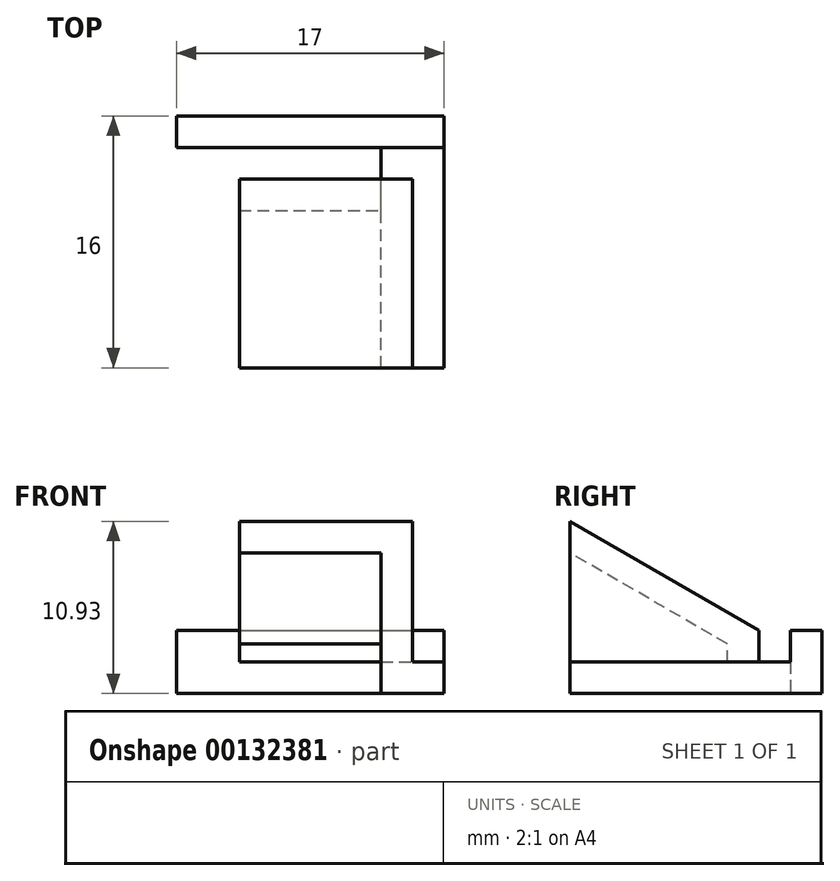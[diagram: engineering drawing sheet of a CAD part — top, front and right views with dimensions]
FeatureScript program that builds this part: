
annotation { "Feature Type Name" : "Feature", "Feature Type Description" : "" }
export const myFeature = defineFeature(function(context is Context, id is Id, definition is map)
    precondition{}
    {
        {
            var Q0;
            Q0=qCreatedBy(makeId("Top.planeOp"),FACE);
            var sketch = newSketch(context, id + "F0", { "sketchPlane" : qUnion([Q0])});
            skCircle(sketch, "E0", {"center": v(0, 0) * mm, "radius": 2.5 * mm});
            skPoint(sketch, "E1", {"position": v(2.5, 0) * mm});
            skPoint(sketch, "E2", {"position": v(-2.5, 0) * mm});
            skLineSegment(sketch, "E3", {"start": v(-2.5, 0) * mm, "end": v(-4.5, 0) * mm, "construction": true});
            skLineSegment(sketch, "E4", {"start": v(2.5, 0) * mm, "end": v(4.5, 0) * mm, "construction": true});
            skPoint(sketch, "E5", {"position": v(0, 2.5) * mm});
            skPoint(sketch, "E6", {"position": v(0, -2.5) * mm});
            skSolve(sketch);
        }
        {
            var Q0;
            Q0=sQuery(id+"F0.wireOp",VERTEX,"E4.end");
            var Q1;
            Q1=qCreatedBy(makeId("Right.planeOp"),FACE);
            cPlane(context, id + "F1", {"entities" : qUnion([Q0, Q1]), "cplaneType" : CPlaneType.PLANE_POINT, "offset" : 25 * mm, "width" : 150 * mm, "height" : 150 * mm});
        }
        {
            var Q0;
            Q0=sQuery(id+"F0.wireOp",VERTEX,"E3.end");
            var Q1;
            Q1=qCreatedBy(makeId("Right.planeOp"),FACE);
            cPlane(context, id + "F2", {"entities" : qUnion([Q0, Q1]), "cplaneType" : CPlaneType.PLANE_POINT, "offset" : 25 * mm, "width" : 150 * mm, "height" : 150 * mm});
        }
        {
            var Q0;
            Q0=qCreatedBy(id+"F1.planeOp",FACE);
            var sketch = newSketch(context, id + "F3", { "sketchPlane" : qUnion([Q0])});
            skLineSegment(sketch, "E7", {"start": v(6.5, 0) * mm, "end": v(6.5, 4) * mm});
            skLineSegment(sketch, "E8", {"start": v(6.5, 4) * mm, "end": v(-5.5, 10.93) * mm});
            skLineSegment(sketch, "E9", {"start": v(-5.5, 10.93) * mm, "end": v(-5.5, 8.93) * mm});
            skLineSegment(sketch, "E10", {"start": v(-5.5, 8.93) * mm, "end": v(4.5, 3.15) * mm});
            skLineSegment(sketch, "E11", {"start": v(4.5, 3.15) * mm, "end": v(4.5, 0) * mm});
            skLineSegment(sketch, "E12", {"start": v(4.5, 0) * mm, "end": v(6.5, 0) * mm});
            skSolve(sketch);
        }
        {
            var Q0;
            Q0 = qSketchRegion(id + "F3", true);
            var Q1;
            Q1=qCreatedBy(id+"F2.planeOp",FACE);
            extrude(context, id + "F4", {"entities" : qUnion([Q0]), "endBound" : BoundingType.UP_TO_SURFACE, "oppositeDirection" : true, "endBoundEntityFace" : qUnion([Q1]), "depth" : 25 * mm});
        }
        {
            var Q0;
            Q0=makeQuery(id+"F4.opExtrude","CAP_FACE",FACE,{"disambiguationData":[OSD([sQuery(id+"F3.wireOp",EDGE,"E7"),sQuery(id+"F3.wireOp",EDGE,"E8"),sQuery(id+"F3.wireOp",EDGE,"E9"),sQuery(id+"F3.wireOp",EDGE,"E10"),sQuery(id+"F3.wireOp",EDGE,"E11"),sQuery(id+"F3.wireOp",EDGE,"E12")])],"isStart":true});
            var sketch = newSketch(context, id + "F5", { "sketchPlane" : qUnion([Q0])});
            skLineSegment(sketch, "E13", {"start": v(-5.5, 10.93) * mm, "end": v(6.5, 4) * mm});
            skLineSegment(sketch, "E14", {"start": v(6.5, 4) * mm, "end": v(6.5, 0) * mm});
            skLineSegment(sketch, "E15", {"start": v(6.5, 0) * mm, "end": v(-5.5, 0) * mm});
            skLineSegment(sketch, "E16", {"start": v(-5.5, 0) * mm, "end": v(-5.5, 10.93) * mm});
            skSolve(sketch);
        }
        {
            var Q0;
            Q0 = qSketchRegion(id + "F5", true);
            extrude(context, id + "F6", {"entities" : qUnion([Q0]), "operationType" : NewBodyOperationType.ADD, "depth" : 2 * mm});
        }
        {
            var Q0;
            Q0=qCreatedBy(makeId("Top.planeOp"),FACE);
            var sketch = newSketch(context, id + "F7", { "sketchPlane" : qUnion([Q0])});
            skLineSegment(sketch, "E17", {"start": v(4.5, 6.5) * mm, "end": v(4.5, 8.5) * mm});
            skLineSegment(sketch, "E18", {"start": v(4.5, 8.5) * mm, "end": v(8.5, 8.5) * mm});
            skLineSegment(sketch, "E19", {"start": v(8.5, 8.5) * mm, "end": v(8.5, -5.5) * mm});
            skLineSegment(sketch, "E20", {"start": v(8.5, -5.5) * mm, "end": v(6.5, -5.5) * mm});
            skLineSegment(sketch, "E21", {"start": v(4.5, 6.5) * mm, "end": v(6.5, 6.5) * mm});
            skLineSegment(sketch, "E22", {"start": v(6.5, 6.5) * mm, "end": v(6.5, -5.5) * mm});
            skSolve(sketch);
        }
        {
            var Q0;
            Q0 = qSketchRegion(id + "F7", true);
            extrude(context, id + "F8", {"entities" : qUnion([Q0]), "operationType" : NewBodyOperationType.ADD, "depth" : 2 * mm});
        }
        {
            var Q0;
            {var subQ0=sQuery(id+"F5.wireOp",EDGE,"E14");Q0=makeQuery(id+"F9clCaSSInO4sDL_1.1.F6.boolean.opBoolean","MERGE",FACE,{"derivedFrom":[makeQuery(id+"F6.boolean.opBoolean","MERGE",FACE,{"derivedFrom":[makeQuery(id+"F4.opExtrude","SWEPT_FACE",FACE,{"disambiguationData":[OSD([sQuery(id+"F3.wireOp",EDGE,"E7")])]}),makeQuery(id+"F6.opExtrude","SWEPT_FACE",FACE,{"disambiguationData":[OSD([subQ0])]})]}),makeQuery(id+"F9clCaSSInO4sDL_1.1.F6.opExtrude","SWEPT_FACE",FACE,{"disambiguationData":[OSD([subQ0])]})]});}
            var sketch = newSketch(context, id + "F9", { "sketchPlane" : qUnion([Q0])});
            skLineSegment(sketch, "E23.bottom", {"start": v(4.5, 2) * mm, "end": v(-4.5, 2) * mm});
            skLineSegment(sketch, "E23.top", {"start": v(4.5, 0) * mm, "end": v(-4.5, 0) * mm});
            skLineSegment(sketch, "E23.left", {"start": v(4.5, 2) * mm, "end": v(4.5, 0) * mm});
            skLineSegment(sketch, "E23.right", {"start": v(-4.5, 2) * mm, "end": v(-4.5, 0) * mm});
            skSolve(sketch);
        }
        {
            var Q0;
            Q0 = qSketchRegion(id + "F9", true);
            extrude(context, id + "F10", {"entities" : qUnion([Q0]), "operationType" : NewBodyOperationType.REMOVE, "endBound" : BoundingType.UP_TO_NEXT, "oppositeDirection" : true, "depth" : 25 * mm});
        }
        {
            var Q0;
            Q0=qCreatedBy(makeId("Top.planeOp"),FACE);
            var sketch = newSketch(context, id + "F11", { "sketchPlane" : qUnion([Q0])});
            skLineSegment(sketch, "E24.bottom", {"start": v(-8.5, 8.5) * mm, "end": v(8.5, 8.5) * mm});
            skLineSegment(sketch, "E24.top", {"start": v(-8.5, 10.5) * mm, "end": v(8.5, 10.5) * mm});
            skLineSegment(sketch, "E24.left", {"start": v(-8.5, 8.5) * mm, "end": v(-8.5, 10.5) * mm});
            skLineSegment(sketch, "E24.right", {"start": v(8.5, 8.5) * mm, "end": v(8.5, 10.5) * mm});
            skSolve(sketch);
        }
        {
            var Q0;
            Q0 = qSketchRegion(id + "F11", true);
            extrude(context, id + "F12", {"entities" : qUnion([Q0]), "operationType" : NewBodyOperationType.ADD, "depth" : 4 * mm});
        }
    });
